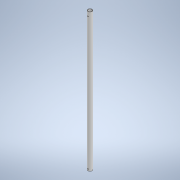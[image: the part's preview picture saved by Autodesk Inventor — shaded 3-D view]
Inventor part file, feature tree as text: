
AUTODESK INVENTOR PART (.ipt)
format: ipt  version: 2022 (Build 260153000, 153)  size: 173,568 bytes
history: native  units: mm
features: extrude x2, sketch x2
ambient origin geometry x8: Origin, YZ Plane, XZ Plane, XY Plane, X Axis, Y Axis, Z Axis, Center Point
bodies: Body1 (feature_tree)
feature tree (4):
  extrude  "Extrusion5"  Depth=15.0mm
  extrude  "Extrusion6"  Depth=10.0mm TaperAngle=0.0deg
  sketch  "Sketch2"  dims[d31=34.456mm d91=15.0mm]
  sketch  "Sketch3"  dims[d92=13.0mm d93=500.0mm d94=0.0mm d95=6.0mm d96=3.0mm d97=20.0mm d98=10.0mm d99=0.0mm d100=0.0mm d101=15.0mm d102=3.0mm]
